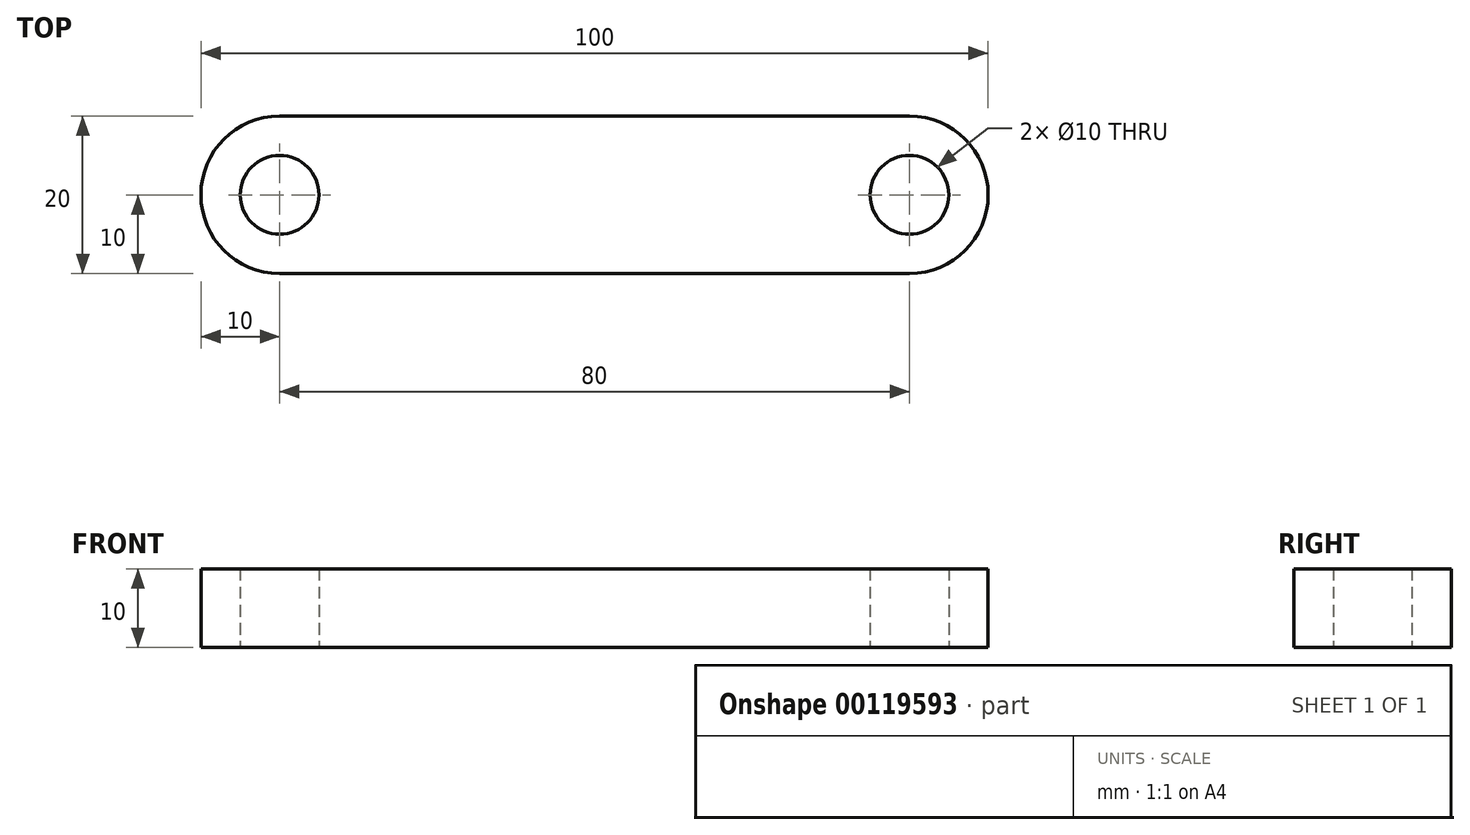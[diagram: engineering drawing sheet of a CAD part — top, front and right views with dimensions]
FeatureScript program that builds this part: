
annotation { "Feature Type Name" : "Feature", "Feature Type Description" : "" }
export const myFeature = defineFeature(function(context is Context, id is Id, definition is map)
    precondition{}
    {
        {
            var Q0;
            Q0=qCreatedBy(makeId("Top.planeOp"),FACE);
            var sketch = newSketch(context, id + "F0", { "sketchPlane" : qUnion([Q0])});
            skCircle(sketch, "E0", {"center": v(0, 0) * mm, "radius": 5 * mm});
            skArc(sketch, "E1", {"start": v(0, 10) * mm, "mid": v(-10, 0) * mm, "end": v(0, -10) * mm});
            skLineSegment(sketch, "E2", {"start": v(0, 10) * mm, "end": v(80, 10) * mm});
            skLineSegment(sketch, "E3", {"start": v(0, -10) * mm, "end": v(80, -10) * mm});
            skArc(sketch, "E4", {"start": v(80, -10) * mm, "mid": v(90, 0) * mm, "end": v(80, 10) * mm});
            skCircle(sketch, "E5", {"center": v(80, 0) * mm, "radius": 5 * mm});
            skSolve(sketch);
        }
        {
            var Q0;
            Q0=makeQuery(id+"F0.imprint","IMPRINT",FACE,{"disambiguationData":[TD([[makeQuery(id+"F0.imprint","IMPRINT",EDGE,{"derivedFrom":sQuery(id+"F0.wireOp",EDGE,"E0")}),-1.0]])]});
            extrude(context, id + "F1", {"entities" : qUnion([Q0]), "depth" : 10 * mm});
        }
    });
